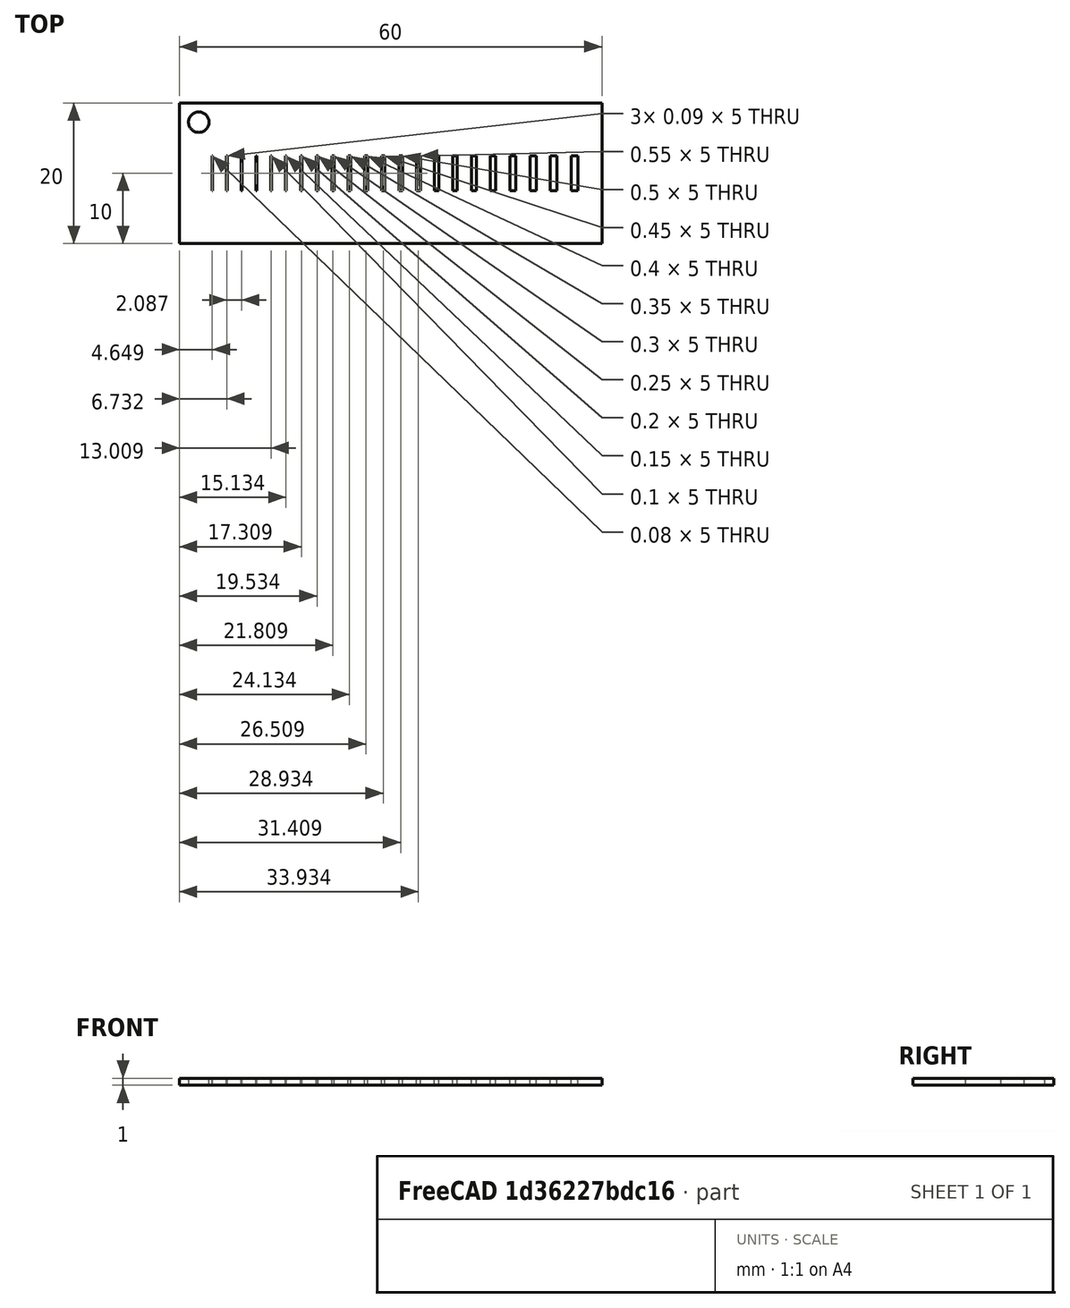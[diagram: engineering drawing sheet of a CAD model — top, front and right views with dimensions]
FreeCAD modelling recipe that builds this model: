
FCSTD DOCUMENT  (FreeCAD 0.20R29177 +233 (Git))
Label: CALIBRATION TEST
License: All rights reserved
LicenseURL: http://en.wikipedia.org/wiki/All_rights_reserved
objects: Sketcher::SketchObject×1, PartDesign::Pad×1, PartDesign::Body×1
note: 4 computed .brp shape members not serialized (recipe doc carries the construction recipe); baked Part::Feature solids carry a one-line shape summary decoded from their .brp

FEATURE [Sketcher::SketchObject] Sketch
  FullyConstrained = false
  MapMode = 5
  Support = -> [XY_Plane]
  sketch-geometry (97):
    g0: LineSegment StartX=-30 StartY=20 StartZ=0 EndX=30 EndY=20 EndZ=0
    g1: LineSegment StartX=30 StartY=20 StartZ=0 EndX=30 EndY=0 EndZ=0
    g2: LineSegment StartX=30 StartY=0 StartZ=0 EndX=-30 EndY=0 EndZ=0
    g3: LineSegment StartX=-30 StartY=0 StartZ=0 EndX=-30 EndY=20 EndZ=0
    g4: LineSegment StartX=-30 StartY=12.5 StartZ=0 EndX=30 EndY=12.5 EndZ=0
    g5: LineSegment StartX=30 StartY=12.5 StartZ=0 EndX=30 EndY=7.5 EndZ=0
    g6: LineSegment StartX=30 StartY=7.5 StartZ=0 EndX=-30 EndY=7.5 EndZ=0
    g7: LineSegment StartX=-30 StartY=7.5 StartZ=0 EndX=-30 EndY=12.5 EndZ=0
    g8: LineSegment StartX=-25.391 StartY=12.5 StartZ=0 EndX=-25.311 EndY=12.5 EndZ=0
    g9: LineSegment StartX=-25.311 StartY=12.5 StartZ=0 EndX=-25.311 EndY=7.5 EndZ=0
    g10: LineSegment StartX=-25.311 StartY=7.5 StartZ=0 EndX=-25.391 EndY=7.5 EndZ=0
    g11: LineSegment StartX=-25.391 StartY=7.5 StartZ=0 EndX=-25.391 EndY=12.5 EndZ=0
    g12: LineSegment StartX=-23.311 StartY=7.5 StartZ=0 EndX=-23.226 EndY=7.5 EndZ=0
    g13: LineSegment StartX=-23.226 StartY=7.5 StartZ=0 EndX=-23.226 EndY=12.5 EndZ=0
    g14: LineSegment StartX=-23.226 StartY=12.5 StartZ=0 EndX=-23.311 EndY=12.5 EndZ=0
    g15: LineSegment StartX=-23.311 StartY=12.5 StartZ=0 EndX=-23.311 EndY=7.5 EndZ=0
    g16: LineSegment StartX=-21.226 StartY=7.5 StartZ=0 EndX=-21.136 EndY=7.5 EndZ=0
    g17: LineSegment StartX=-21.136 StartY=7.5 StartZ=0 EndX=-21.136 EndY=12.5 EndZ=0
    g18: LineSegment StartX=-21.136 StartY=12.5 StartZ=0 EndX=-21.226 EndY=12.5 EndZ=0
    g19: LineSegment StartX=-21.226 StartY=12.5 StartZ=0 EndX=-21.226 EndY=7.5 EndZ=0
    g20: LineSegment StartX=-19.136 StartY=7.5 StartZ=0 EndX=-19.041 EndY=7.5 EndZ=0
    g21: LineSegment StartX=-19.041 StartY=7.5 StartZ=0 EndX=-19.041 EndY=12.5 EndZ=0
    g22: LineSegment StartX=-19.041 StartY=12.5 StartZ=0 EndX=-19.136 EndY=12.5 EndZ=0
    g23: LineSegment StartX=-19.136 StartY=12.5 StartZ=0 EndX=-19.136 EndY=7.5 EndZ=0
    g24: LineSegment StartX=-17.041 StartY=7.5 StartZ=0 EndX=-16.941 EndY=7.5 EndZ=0
    g25: LineSegment StartX=-16.941 StartY=7.5 StartZ=0 EndX=-16.941 EndY=12.5 EndZ=0
    g26: LineSegment StartX=-16.941 StartY=12.5 StartZ=0 EndX=-17.041 EndY=12.5 EndZ=0
    g27: LineSegment StartX=-17.041 StartY=12.5 StartZ=0 EndX=-17.041 EndY=7.5 EndZ=0
    g28: LineSegment StartX=-14.941 StartY=7.5 StartZ=0 EndX=-14.791 EndY=7.5 EndZ=0
    g29: LineSegment StartX=-14.791 StartY=7.5 StartZ=0 EndX=-14.791 EndY=12.5 EndZ=0
    g30: LineSegment StartX=-14.791 StartY=12.5 StartZ=0 EndX=-14.941 EndY=12.5 EndZ=0
    g31: LineSegment StartX=-14.941 StartY=12.5 StartZ=0 EndX=-14.941 EndY=7.5 EndZ=0
    g32: LineSegment StartX=-12.791 StartY=7.5 StartZ=0 EndX=-12.591 EndY=7.5 EndZ=0
    g33: LineSegment StartX=-12.591 StartY=7.5 StartZ=0 EndX=-12.591 EndY=12.5 EndZ=0
    g34: LineSegment StartX=-12.591 StartY=12.5 StartZ=0 EndX=-12.791 EndY=12.5 EndZ=0
    g35: LineSegment StartX=-12.791 StartY=12.5 StartZ=0 EndX=-12.791 EndY=7.5 EndZ=0
    g36: LineSegment StartX=-10.591 StartY=7.5 StartZ=0 EndX=-10.341 EndY=7.5 EndZ=0
    g37: LineSegment StartX=-10.341 StartY=7.5 StartZ=0 EndX=-10.341 EndY=12.5 EndZ=0
    g38: LineSegment StartX=-10.341 StartY=12.5 StartZ=0 EndX=-10.591 EndY=12.5 EndZ=0
    g39: LineSegment StartX=-10.591 StartY=12.5 StartZ=0 EndX=-10.591 EndY=7.5 EndZ=0
    g40: LineSegment StartX=-8.34095 StartY=12.5 StartZ=0 EndX=-8.04095 EndY=12.5 EndZ=0
    g41: LineSegment StartX=-8.04095 StartY=12.5 StartZ=0 EndX=-8.04095 EndY=7.5 EndZ=0
    g42: LineSegment StartX=-8.04095 StartY=7.5 StartZ=0 EndX=-8.34095 EndY=7.5 EndZ=0
    g43: LineSegment StartX=-8.34095 StartY=7.5 StartZ=0 EndX=-8.34095 EndY=12.5 EndZ=0
    g44: LineSegment StartX=-6.04095 StartY=12.5 StartZ=0 EndX=-5.69095 EndY=12.5 EndZ=0
    g45: LineSegment StartX=-5.69095 StartY=12.5 StartZ=0 EndX=-5.69095 EndY=7.5 EndZ=0
    g46: LineSegment StartX=-5.69095 StartY=7.5 StartZ=0 EndX=-6.04095 EndY=7.5 EndZ=0
    g47: LineSegment StartX=-6.04095 StartY=7.5 StartZ=0 EndX=-6.04095 EndY=12.5 EndZ=0
    g48: LineSegment StartX=-3.69095 StartY=12.5 StartZ=0 EndX=-3.29095 EndY=12.5 EndZ=0
    g49: LineSegment StartX=-3.29095 StartY=12.5 StartZ=0 EndX=-3.29095 EndY=7.5 EndZ=0
    g50: LineSegment StartX=-3.29095 StartY=7.5 StartZ=0 EndX=-3.69095 EndY=7.5 EndZ=0
    g51: LineSegment StartX=-3.69095 StartY=7.5 StartZ=0 EndX=-3.69095 EndY=12.5 EndZ=0
    g52: LineSegment StartX=-1.29095 StartY=12.5 StartZ=0 EndX=-0.840953 EndY=12.5 EndZ=0
    g53: LineSegment StartX=-0.840953 StartY=12.5 StartZ=0 EndX=-0.840953 EndY=7.5 EndZ=0
    g54: LineSegment StartX=-0.840953 StartY=7.5 StartZ=0 EndX=-1.29095 EndY=7.5 EndZ=0
    g55: LineSegment StartX=-1.29095 StartY=7.5 StartZ=0 EndX=-1.29095 EndY=12.5 EndZ=0
    g56: LineSegment StartX=1.15905 StartY=12.5 StartZ=0 EndX=1.65905 EndY=12.5 EndZ=0
    g57: LineSegment StartX=1.65905 StartY=12.5 StartZ=0 EndX=1.65905 EndY=7.5 EndZ=0
    g58: LineSegment StartX=1.65905 StartY=7.5 StartZ=0 EndX=1.15905 EndY=7.5 EndZ=0
    g59: LineSegment StartX=1.15905 StartY=7.5 StartZ=0 EndX=1.15905 EndY=12.5 EndZ=0
    g60: LineSegment StartX=3.65905 StartY=12.5 StartZ=0 EndX=4.20905 EndY=12.5 EndZ=0
    g61: LineSegment StartX=4.20905 StartY=12.5 StartZ=0 EndX=4.20905 EndY=7.5 EndZ=0
    g62: LineSegment StartX=4.20905 StartY=7.5 StartZ=0 EndX=3.65905 EndY=7.5 EndZ=0
    g63: LineSegment StartX=3.65905 StartY=7.5 StartZ=0 EndX=3.65905 EndY=12.5 EndZ=0
    g64: LineSegment StartX=6.20905 StartY=12.5 StartZ=0 EndX=6.80905 EndY=12.5 EndZ=0
    g65: LineSegment StartX=6.80905 StartY=12.5 StartZ=0 EndX=6.80905 EndY=7.5 EndZ=0
    g66: LineSegment StartX=6.80905 StartY=7.5 StartZ=0 EndX=6.20905 EndY=7.5 EndZ=0
    g67: LineSegment StartX=6.20905 StartY=7.5 StartZ=0 EndX=6.20905 EndY=12.5 EndZ=0
    g68: LineSegment StartX=8.80905 StartY=12.5 StartZ=0 EndX=9.45905 EndY=12.5 EndZ=0
    g69: LineSegment StartX=9.45905 StartY=12.5 StartZ=0 EndX=9.45905 EndY=7.5 EndZ=0
    g70: LineSegment StartX=9.45905 StartY=7.5 StartZ=0 EndX=8.80905 EndY=7.5 EndZ=0
    g71: LineSegment StartX=8.80905 StartY=7.5 StartZ=0 EndX=8.80905 EndY=12.5 EndZ=0
    g72: LineSegment StartX=11.459 StartY=12.5 StartZ=0 EndX=12.159 EndY=12.5 EndZ=0
    g73: LineSegment StartX=12.159 StartY=12.5 StartZ=0 EndX=12.159 EndY=7.5 EndZ=0
    g74: LineSegment StartX=12.159 StartY=7.5 StartZ=0 EndX=11.459 EndY=7.5 EndZ=0
    g75: LineSegment StartX=11.459 StartY=7.5 StartZ=0 EndX=11.459 EndY=12.5 EndZ=0
    g76: LineSegment StartX=14.159 StartY=12.5 StartZ=0 EndX=14.909 EndY=12.5 EndZ=0
    g77: LineSegment StartX=14.909 StartY=12.5 StartZ=0 EndX=14.909 EndY=7.5 EndZ=0
    g78: LineSegment StartX=14.909 StartY=7.5 StartZ=0 EndX=14.159 EndY=7.5 EndZ=0
    g79: LineSegment StartX=14.159 StartY=7.5 StartZ=0 EndX=14.159 EndY=12.5 EndZ=0
    g80: LineSegment StartX=16.909 StartY=12.5 StartZ=0 EndX=17.759 EndY=12.5 EndZ=0
    g81: LineSegment StartX=17.759 StartY=12.5 StartZ=0 EndX=17.759 EndY=7.5 EndZ=0
    g82: LineSegment StartX=17.759 StartY=7.5 StartZ=0 EndX=16.909 EndY=7.5 EndZ=0
    g83: LineSegment StartX=16.909 StartY=7.5 StartZ=0 EndX=16.909 EndY=12.5 EndZ=0
    g84: LineSegment StartX=19.759 StartY=12.5 StartZ=0 EndX=20.659 EndY=12.5 EndZ=0
    g85: LineSegment StartX=20.659 StartY=12.5 StartZ=0 EndX=20.659 EndY=7.5 EndZ=0
    g86: LineSegment StartX=20.659 StartY=7.5 StartZ=0 EndX=19.759 EndY=7.5 EndZ=0
    g87: LineSegment StartX=19.759 StartY=7.5 StartZ=0 EndX=19.759 EndY=12.5 EndZ=0
    g88: LineSegment StartX=22.659 StartY=12.5 StartZ=0 EndX=23.609 EndY=12.5 EndZ=0
    g89: LineSegment StartX=23.609 StartY=12.5 StartZ=0 EndX=23.609 EndY=7.5 EndZ=0
    g90: LineSegment StartX=23.609 StartY=7.5 StartZ=0 EndX=22.659 EndY=7.5 EndZ=0
    g91: LineSegment StartX=22.659 StartY=7.5 StartZ=0 EndX=22.659 EndY=12.5 EndZ=0
    g92: LineSegment StartX=25.609 StartY=7.5 StartZ=0 EndX=26.609 EndY=7.5 EndZ=0
    g93: LineSegment StartX=26.609 StartY=7.5 StartZ=0 EndX=26.609 EndY=12.5 EndZ=0
    g94: LineSegment StartX=26.609 StartY=12.5 StartZ=0 EndX=25.609 EndY=12.5 EndZ=0
    g95: LineSegment StartX=25.609 StartY=12.5 StartZ=0 EndX=25.609 EndY=7.5 EndZ=0
    g96: Circle CenterX=-27.2497 CenterY=17.2558 CenterZ=0 NormalX=0 NormalY=0 NormalZ=1 AngleXU=0 Radius=1.45498
  constraints (286):
    c: Coincident(g0,g1)
    c: Coincident(g1,g2)
    c: Coincident(g2,g3)
    c: Coincident(g3,g0)
    c: Horizontal(g0)
    c: Horizontal(g2)
    c: Vertical(g1)
    c: Vertical(g3)
    c: Symmetric(g2,g1,g-1)
    c: DistanceX(g0,g0) = 60
    c: DistanceY(g1,g1) = 20
    c: Coincident(g4,g5)
    c: Coincident(g5,g6)
    c: Coincident(g6,g7)
    c: Coincident(g7,g4)
    c: Horizontal(g4)
    c: Horizontal(g6)
    c: Vertical(g5)
    c: Vertical(g7)
    c: PointOnObject(g4,g3)
    c: PointOnObject(g5,g1)
    c: DistanceY(g5,g4) = 5
    c: DistanceY(g1,g5) = 7.5
    c: Coincident(g8,g9)
    c: Coincident(g9,g10)
    c: Coincident(g10,g11)
    c: Coincident(g11,g8)
    c: Horizontal(g8)
    c: Horizontal(g10)
    c: Vertical(g9)
    c: Vertical(g11)
    c: PointOnObject(g8,g4)
    c: PointOnObject(g9,g6)
    c: DistanceX(g8,g8) = 0.08
    c: Coincident(g12,g13)
    c: Coincident(g13,g14)
    c: Coincident(g14,g15)
    c: Coincident(g15,g12)
    c: Horizontal(g12)
    c: Horizontal(g14)
    c: Vertical(g13)
    c: Vertical(g15)
    c: PointOnObject(g12,g6)
    c: PointOnObject(g13,g4)
    c: Coincident(g16,g17)
    c: Coincident(g17,g18)
    c: Coincident(g18,g19)
    c: Coincident(g19,g16)
    c: Horizontal(g16)
    c: Horizontal(g18)
    c: Vertical(g17)
    c: Vertical(g19)
    c: PointOnObject(g16,g6)
    c: PointOnObject(g17,g4)
    c: Coincident(g20,g21)
    c: Coincident(g21,g22)
    c: Coincident(g22,g23)
    c: Coincident(g23,g20)
    c: Horizontal(g20)
    c: Horizontal(g22)
    c: Vertical(g21)
    c: Vertical(g23)
    c: PointOnObject(g20,g6)
    c: PointOnObject(g21,g4)
    c: Coincident(g24,g25)
    c: Coincident(g25,g26)
    c: Coincident(g26,g27)
    c: Coincident(g27,g24)
    c: Horizontal(g24)
    c: Horizontal(g26)
    c: Vertical(g25)
    c: Vertical(g27)
    c: PointOnObject(g24,g6)
    c: PointOnObject(g25,g4)
    c: Coincident(g28,g29)
    c: Coincident(g29,g30)
    c: Coincident(g30,g31)
    c: Coincident(g31,g28)
    c: Horizontal(g28)
    c: Horizontal(g30)
    c: Vertical(g29)
    c: Vertical(g31)
    c: PointOnObject(g28,g6)
    c: PointOnObject(g29,g4)
    c: Coincident(g32,g33)
    c: Coincident(g33,g34)
    c: Coincident(g34,g35)
    c: Coincident(g35,g32)
    c: Horizontal(g32)
    c: Horizontal(g34)
    c: Vertical(g33)
    c: Vertical(g35)
    c: PointOnObject(g32,g6)
    c: PointOnObject(g33,g4)
    c: Coincident(g36,g37)
    c: Coincident(g37,g38)
    c: Coincident(g38,g39)
    c: Coincident(g39,g36)
    c: Horizontal(g36)
    c: Horizontal(g38)
    c: Vertical(g37)
    c: Vertical(g39)
    c: PointOnObject(g37,g4)
    c: DistanceX(g14,g14) = 0.085
    c: DistanceX(g18,g18) = 0.09
    c: DistanceX(g20,g20) = 0.095
    c: DistanceX(g26,g26) = 0.1
    c: DistanceX(g30,g30) = 0.15
    c: DistanceX(g34,g34) = 0.2
    c: DistanceX(g38,g38) = 0.25
    c: PointOnObject(g36,g6)
    c: Coincident(g40,g41)
    c: Coincident(g41,g42)
    c: Coincident(g42,g43)
    c: Coincident(g43,g40)
    c: Horizontal(g40)
    c: Horizontal(g42)
    c: Vertical(g41)
    c: Vertical(g43)
    c: PointOnObject(g40,g4)
    c: PointOnObject(g41,g6)
    c: Coincident(g44,g45)
    c: Coincident(g45,g46)
    c: Coincident(g46,g47)
    c: Coincident(g47,g44)
    c: Horizontal(g44)
    c: Horizontal(g46)
    c: Vertical(g45)
    c: Vertical(g47)
    c: PointOnObject(g44,g4)
    c: PointOnObject(g45,g6)
    c: Coincident(g48,g49)
    c: Coincident(g49,g50)
    c: Coincident(g50,g51)
    c: Coincident(g51,g48)
    c: Horizontal(g48)
    c: Horizontal(g50)
    c: Vertical(g49)
    c: Vertical(g51)
    c: PointOnObject(g48,g4)
    c: PointOnObject(g49,g6)
    c: Coincident(g52,g53)
    c: Coincident(g53,g54)
    c: Coincident(g54,g55)
    c: Coincident(g55,g52)
    c: Horizontal(g52)
    c: Horizontal(g54)
    c: Vertical(g53)
    c: Vertical(g55)
    c: PointOnObject(g52,g4)
    c: PointOnObject(g53,g6)
    c: Coincident(g56,g57)
    c: Coincident(g57,g58)
    c: Coincident(g58,g59)
    c: Coincident(g59,g56)
    c: Horizontal(g56)
    c: Horizontal(g58)
    c: Vertical(g57)
    c: Vertical(g59)
    c: PointOnObject(g56,g4)
    c: PointOnObject(g57,g6)
    c: Coincident(g60,g61)
    c: Coincident(g61,g62)
    c: Coincident(g62,g63)
    c: Coincident(g63,g60)
    c: Horizontal(g60)
    c: Horizontal(g62)
    c: Vertical(g61)
    c: Vertical(g63)
    c: PointOnObject(g60,g4)
    c: PointOnObject(g61,g6)
    c: Coincident(g64,g65)
    c: Coincident(g65,g66)
    c: Coincident(g66,g67)
    c: Coincident(g67,g64)
    c: Horizontal(g64)
    c: Horizontal(g66)
    c: Vertical(g65)
    c: Vertical(g67)
    c: PointOnObject(g64,g4)
    c: PointOnObject(g65,g6)
    c: Coincident(g68,g69)
    c: Coincident(g69,g70)
    c: Coincident(g70,g71)
    c: Coincident(g71,g68)
    c: Horizontal(g68)
    c: Horizontal(g70)
    c: Vertical(g69)
    c: Vertical(g71)
    c: PointOnObject(g68,g4)
    c: PointOnObject(g69,g6)
    c: Coincident(g72,g73)
    c: Coincident(g73,g74)
    c: Coincident(g74,g75)
    c: Coincident(g75,g72)
    c: Horizontal(g72)
    c: Horizontal(g74)
    c: Vertical(g73)
    c: Vertical(g75)
    c: PointOnObject(g72,g4)
    c: PointOnObject(g73,g6)
    c: Coincident(g76,g77)
    c: Coincident(g77,g78)
    c: Coincident(g78,g79)
    c: Coincident(g79,g76)
    c: Horizontal(g76)
    c: Horizontal(g78)
    c: Vertical(g77)
    c: Vertical(g79)
    c: PointOnObject(g76,g4)
    c: PointOnObject(g77,g6)
    c: Coincident(g80,g81)
    c: Coincident(g81,g82)
    c: Coincident(g82,g83)
    c: Coincident(g83,g80)
    c: Horizontal(g80)
    c: Horizontal(g82)
    c: Vertical(g81)
    c: Vertical(g83)
    c: PointOnObject(g80,g4)
    c: PointOnObject(g81,g6)
    c: Coincident(g84,g85)
    c: Coincident(g85,g86)
    c: Coincident(g86,g87)
    c: Coincident(g87,g84)
    c: Horizontal(g84)
    c: Horizontal(g86)
    c: Vertical(g85)
    c: Vertical(g87)
    c: PointOnObject(g84,g4)
    c: PointOnObject(g85,g6)
    c: Coincident(g88,g89)
    c: Coincident(g89,g90)
    c: Coincident(g90,g91)
    c: Coincident(g91,g88)
    c: Horizontal(g88)
    c: Horizontal(g90)
    c: Vertical(g89)
    c: Vertical(g91)
    c: PointOnObject(g88,g4)
    c: PointOnObject(g89,g6)
    c: DistanceX(g40,g40) = 0.3
    c: DistanceX(g44,g44) = 0.35
    c: DistanceX(g48,g48) = 0.4
    c: DistanceX(g52,g52) = 0.45
    c: DistanceX(g56,g56) = 0.5
    c: DistanceX(g60,g60) = 0.55
    c: DistanceX(g64,g64) = 0.6
    c: DistanceX(g68,g68) = 0.65
    c: DistanceX(g72,g72) = 0.7
    c: DistanceX(g76,g76) = 0.75
    c: DistanceX(g80,g80) = 0.85
    c: DistanceX(g84,g84) = 0.9
    c: DistanceX(g88,g88) = 0.95
    c: Coincident(g92,g93)
    c: Coincident(g93,g94)
    c: Coincident(g94,g95)
    c: Coincident(g95,g92)
    c: Horizontal(g92)
    c: Horizontal(g94)
    c: Vertical(g93)
    c: Vertical(g95)
    c: PointOnObject(g92,g6)
    c: PointOnObject(g93,g4)
    c: DistanceX(g94,g94) = 1
    c: DistanceX(g88,g94) = 2
    c: DistanceX(g84,g88) = 2
    c: DistanceX(g80,g84) = 2
    c: DistanceX(g76,g80) = 2
    c: DistanceX(g72,g76) = 2
    c: DistanceX(g68,g72) = 2
    c: DistanceX(g64,g68) = 2
    c: DistanceX(g60,g64) = 2
    c: DistanceX(g56,g60) = 2
    c: DistanceX(g52,g56) = 2
    c: DistanceX(g48,g52) = 2
    c: DistanceX(g44,g48) = 2
    c: DistanceX(g40,g44) = 2
    c: DistanceX(g37,g40) = 2
    c: DistanceX(g33,g38) = 2
    c: DistanceX(g29,g34) = 2
    c: DistanceX(g25,g30) = 2
    c: DistanceX(g21,g26) = 2
    c: DistanceX(g17,g22) = 2
    c: DistanceX(g13,g18) = 2
    c: DistanceX(g8,g14) = 2
FEATURE [PartDesign::Pad] Pad
  Direction = (0,0,1)
  Length = 1
  Length2 = 10
  Profile = -> Sketch
  ReferenceAxis = -> Sketch [N_Axis]
  Type = 0
FEATURE [PartDesign::Body] Body
  Group = -> [Sketch,Pad]
  Origin = -> Origin
  Tip = -> Pad
